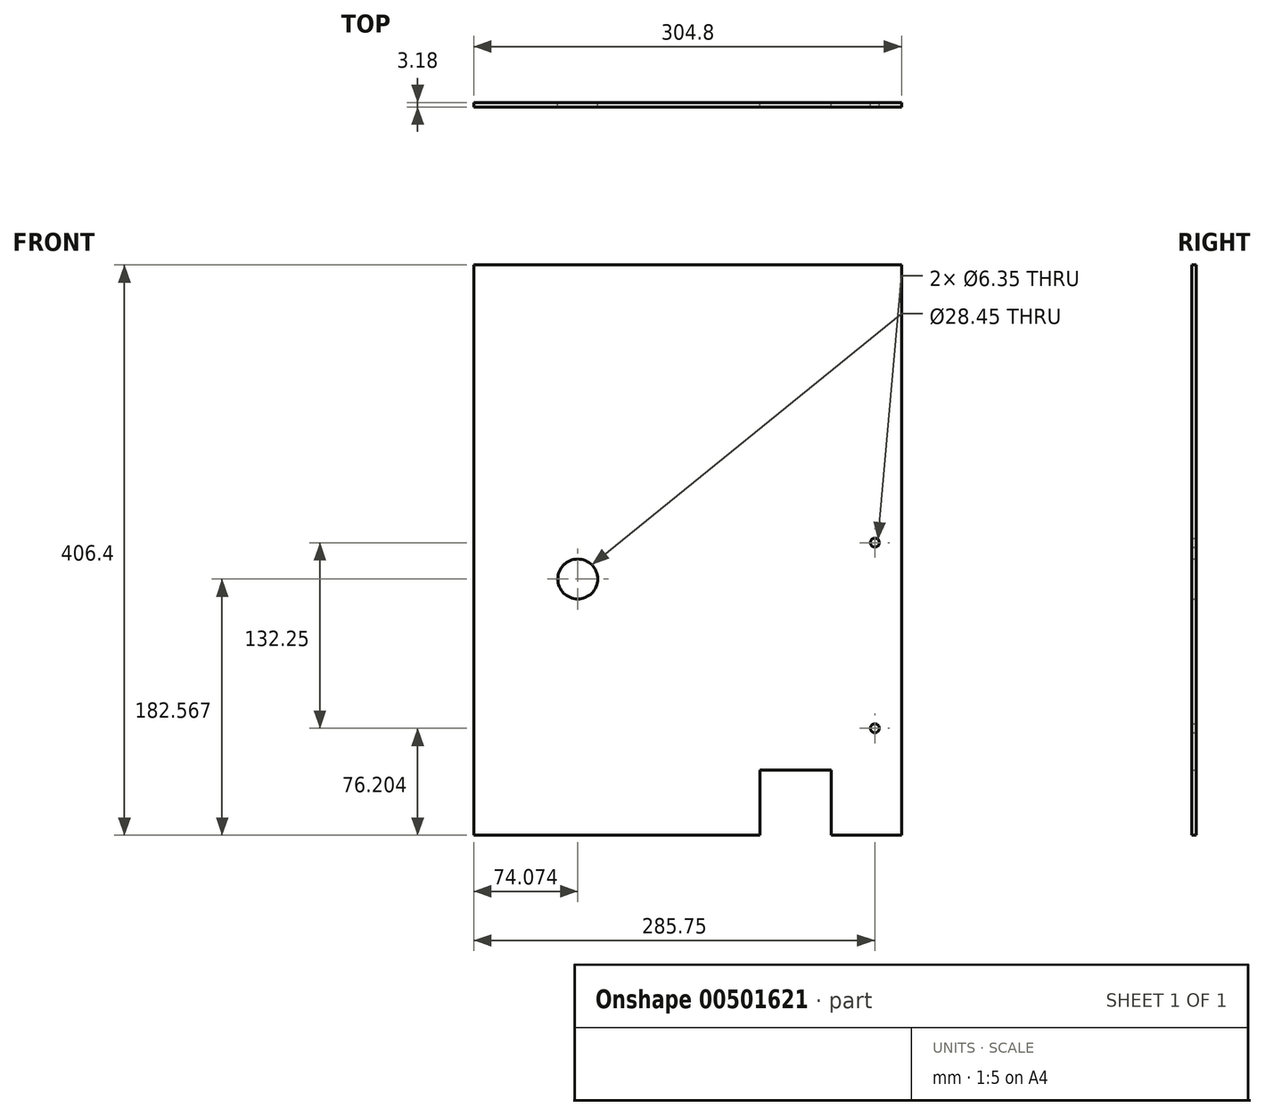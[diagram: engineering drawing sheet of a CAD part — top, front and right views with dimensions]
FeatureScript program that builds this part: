
annotation { "Feature Type Name" : "Feature", "Feature Type Description" : "" }
export const myFeature = defineFeature(function(context is Context, id is Id, definition is map)
    precondition{}
    {
        {
            var Q0;
            Q0=qCreatedBy(makeId("Front.planeOp"),FACE);
            var sketch = newSketch(context, id + "F0", { "sketchPlane" : qUnion([Q0])});
            skArc(sketch, "E0", {"start": v(-147.52, -114.98) * mm, "mid": v(13.68, -18.12) * mm, "end": v(3.84, 169.67) * mm});
            skCircle(sketch, "E1", {"center": v(-147.52, 67.59) * mm, "radius": 61.91 * mm, "construction": true});
            skLineSegment(sketch, "E2", {"start": v(-147.52, 67.59) * mm, "end": v(-147.52, -231.24) * mm, "construction": true});
            skLineSegment(sketch, "E3", {"start": v(-147.52, -114.98) * mm, "end": v(-15.93, -114.98) * mm});
            skLineSegment(sketch, "E4", {"start": v(83.21, -114.98) * mm, "end": v(83.21, 169.67) * mm});
            skLineSegment(sketch, "E5", {"start": v(83.21, 169.67) * mm, "end": v(3.84, 169.67) * mm});
            skLineSegment(sketch, "E6", {"start": v(-147.52, 67.59) * mm, "end": v(230.08, 67.59) * mm, "construction": true});
            skLineSegment(sketch, "E7", {"start": v(35.05, 67.59) * mm, "end": v(3.84, 169.67) * mm, "construction": true});
            skLineSegment(sketch, "E8", {"start": v(35.05, 67.59) * mm, "end": v(35.05, 321.59) * mm, "construction": true});
            skCircle(sketch, "E9", {"center": v(25.86, 150.28) * mm, "radius": 3.18 * mm, "construction": true});
            skCircle(sketch, "E10.1.0", {"center": v(44.04, 81.82) * mm, "radius": 3.18 * mm, "construction": true});
            skCircle(sketch, "E10.2.0", {"center": v(36.18, 11.43) * mm, "radius": 3.18 * mm, "construction": true});
            skCircle(sketch, "E10.3.0", {"center": v(3.33, -51.33) * mm, "radius": 3.18 * mm, "construction": true});
            skCircle(sketch, "E10.4.0", {"center": v(-50.02, -97.92) * mm, "radius": 3.18 * mm, "construction": true});
            skLineSegment(sketch, "E10.anchor1", {"start": v(-147.52, 67.59) * mm, "end": v(25.86, 150.28) * mm, "construction": true});
            skLineSegment(sketch, "E10.anchor2", {"start": v(-147.52, 67.59) * mm, "end": v(-50.02, -97.92) * mm, "construction": true});
            skLineSegment(sketch, "E11.bottom", {"start": v(-15.3, -70.37) * mm, "end": v(30.43, -70.37) * mm});
            skLineSegment(sketch, "E11.left", {"start": v(-15.93, -71) * mm, "end": v(-15.93, -114.98) * mm});
            skLineSegment(sketch, "E11.right", {"start": v(31.06, -71) * mm, "end": v(31.06, -114.98) * mm});
            skLineSegment(sketch, "E12", {"start": v(7.57, -70.37) * mm, "end": v(7.57, -114.98) * mm, "construction": true});
            skPoint(sketch, "E13", {"position": v(7.57, -92.67) * mm});
            skLineSegment(sketch, "E14.trimOffspring", {"start": v(31.06, -114.98) * mm, "end": v(83.21, -114.98) * mm});
            skPoint(sketch, "E15.visualSharp", {"position": v(-15.93, -70.37) * mm});
            skArc(sketch, "E15.filletArc", {"start": v(-15.3, -70.37) * mm, "mid": v(-15.74, -70.56) * mm, "end": v(-15.93, -71) * mm});
            skPoint(sketch, "E16.visualSharp", {"position": v(31.06, -70.37) * mm});
            skArc(sketch, "E16.filletArc", {"start": v(31.06, -71) * mm, "mid": v(30.88, -70.56) * mm, "end": v(30.43, -70.37) * mm});
            skLineSegment(sketch, "E17", {"start": v(64.16, 169.67) * mm, "end": v(64.16, -114.98) * mm, "construction": true});
            skLineSegment(sketch, "E18", {"start": v(83.21, 93.47) * mm, "end": v(33.2, 93.47) * mm, "construction": true});
            skLineSegment(sketch, "E19", {"start": v(0.86, -38.78) * mm, "end": v(83.21, -38.78) * mm, "construction": true});
            skCircle(sketch, "E20", {"center": v(64.16, -38.78) * mm, "radius": 3.18 * mm});
            skCircle(sketch, "E21", {"center": v(64.16, 93.47) * mm, "radius": 3.18 * mm});
            skSolve(sketch);
        }
        {
            var Q0;
            Q0=qCreatedBy(makeId("Front.planeOp"),FACE);
            var sketch = newSketch(context, id + "F1", { "sketchPlane" : qUnion([Q0])});
            skPoint(sketch, "E22.0", {"position": v(-147.52, 67.59) * mm});
            skPoint(sketch, "E23.0", {"position": v(83.21, -114.98) * mm});
            skLineSegment(sketch, "E24.bottom", {"start": v(83.21, -114.98) * mm, "end": v(32.97, -114.98) * mm});
            skLineSegment(sketch, "E24.top", {"start": v(83.21, 291.42) * mm, "end": v(-221.59, 291.42) * mm});
            skLineSegment(sketch, "E24.left", {"start": v(83.21, -114.98) * mm, "end": v(83.21, 291.42) * mm});
            skLineSegment(sketch, "E24.right", {"start": v(-221.59, -114.98) * mm, "end": v(-221.59, 291.42) * mm});
            skCircle(sketch, "E25", {"center": v(-147.52, 67.59) * mm, "radius": 14.22 * mm});
            skPoint(sketch, "E26.middle", {"position": v(7.57, -92.67) * mm});
            skLineSegment(sketch, "E27.trimOffspring", {"start": v(-17.83, -114.98) * mm, "end": v(-221.59, -114.98) * mm});
            skCircle(sketch, "E28.0", {"center": v(64.16, 93.47) * mm, "radius": 3.18 * mm});
            skCircle(sketch, "E28.1", {"center": v(64.16, -38.78) * mm, "radius": 3.18 * mm});
            skLineSegment(sketch, "E29.top", {"start": v(32.97, -68.54) * mm, "end": v(-17.83, -68.54) * mm});
            skLineSegment(sketch, "E29.left", {"start": v(32.97, -114.98) * mm, "end": v(32.97, -68.54) * mm});
            skLineSegment(sketch, "E29.right", {"start": v(-17.83, -114.98) * mm, "end": v(-17.83, -68.54) * mm});
            skPoint(sketch, "E30.orphan", {"position": v(-17.83, -116.8) * mm});
            skPoint(sketch, "E31.orphan", {"position": v(32.97, -116.8) * mm});
            skSolve(sketch);
        }
        {
            var Q0;
            Q0=makeQuery(id+"F1.imprint","IMPRINT",FACE,{"disambiguationData":[TD([[makeQuery(id+"F1.imprint","IMPRINT",EDGE,{"derivedFrom":sQuery(id+"F1.wireOp",EDGE,"E24.bottom")}),-1.0]])]});
            extrude(context, id + "F2", {"entities" : qUnion([Q0]), "depth" : 3.17 * mm});
        }
    });
